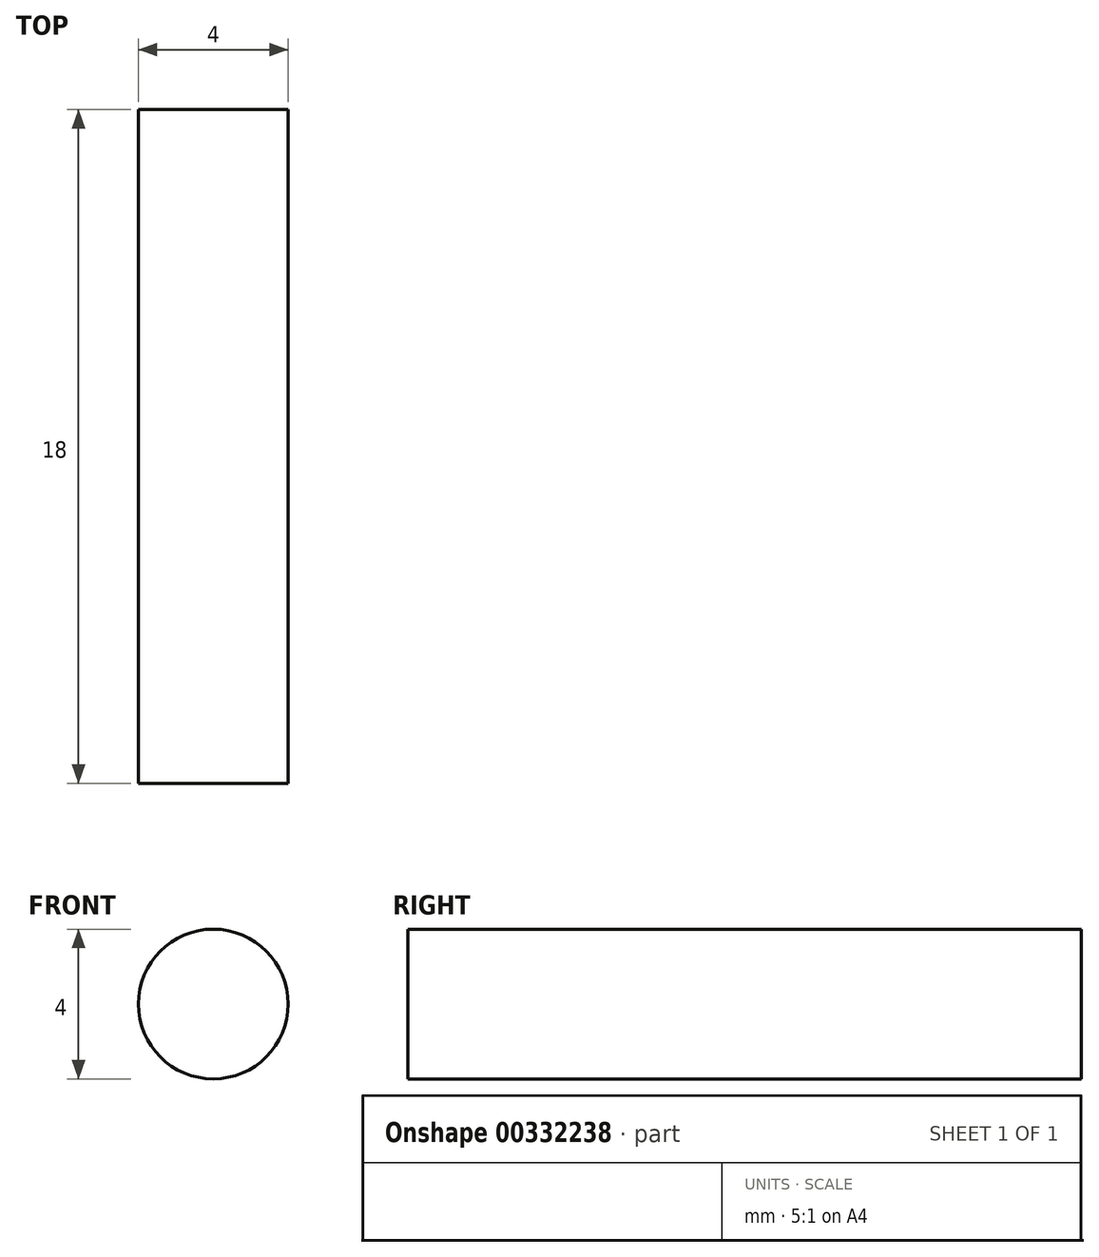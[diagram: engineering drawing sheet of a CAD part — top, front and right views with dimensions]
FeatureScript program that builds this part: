
annotation { "Feature Type Name" : "Feature", "Feature Type Description" : "" }
export const myFeature = defineFeature(function(context is Context, id is Id, definition is map)
    precondition{}
    {
        {
            var Q0;
            Q0=qCreatedBy(makeId("Front.planeOp"),FACE);
            var sketch = newSketch(context, id + "F0", { "sketchPlane" : qUnion([Q0])});
            skCircle(sketch, "E0", {"center": v(-47.7, 27.45) * mm, "radius": 2 * mm});
            skSolve(sketch);
        }
        {
            var Q0;
            Q0=makeQuery(id+"F0.imprint","IMPRINT",FACE,{"disambiguationData":[TD([[makeQuery(id+"F0.imprint","IMPRINT",EDGE,{"derivedFrom":sQuery(id+"F0.wireOp",EDGE,"E0")}),1.0]])]});
            extrude(context, id + "F1", {"entities" : qUnion([Q0]), "depth" : 63 * mm});
        }
        {
            var Q0;
            Q0=makeQuery(id+"F1.opExtrude","CAP_FACE",FACE,{"disambiguationData":[OSD([sQuery(id+"F0.wireOp",EDGE,"E0")])],"isStart":false});
            extrude(context, id + "F2", {"entities" : qUnion([Q0]), "operationType" : NewBodyOperationType.REMOVE, "oppositeDirection" : true, "depth" : 50 * mm});
        }
        {
            var Q0;
            Q0=makeQuery(id+"F2.boolean.opBoolean","COPY",FACE,{"derivedFrom":makeQuery(id+"F2.opExtrude","CAP_FACE",FACE,{"disambiguationData":[OSD([sQuery(id+"F0.wireOp",EDGE,"E0")])],"isStart":false})});
            extrude(context, id + "F3", {"entities" : qUnion([Q0]), "operationType" : NewBodyOperationType.ADD, "depth" : 15 * mm});
        }
        {
            var Q0;
            Q0=makeQuery(id+"F3.opExtrude","CAP_FACE",FACE,{"disambiguationData":[OSD([sQuery(id+"F0.wireOp",EDGE,"E0")])],"isStart":false});
            extrude(context, id + "F4", {"entities" : qUnion([Q0]), "operationType" : NewBodyOperationType.REMOVE, "oppositeDirection" : true, "depth" : 10 * mm});
        }
        {
            var Q0;
            Q0=makeQuery(id+"F4.boolean.opBoolean","COPY",FACE,{"derivedFrom":makeQuery(id+"F4.opExtrude","CAP_FACE",FACE,{"disambiguationData":[OSD([sQuery(id+"F0.wireOp",EDGE,"E0")])],"isStart":false})});
            extrude(context, id + "F5", {"entities" : qUnion([Q0]), "operationType" : NewBodyOperationType.REMOVE, "oppositeDirection" : true, "depth" : 1 * mm});
        }
        {
            var Q0;
            Q0=makeQuery(id+"F5.boolean.opBoolean","COPY",FACE,{"derivedFrom":makeQuery(id+"F5.opExtrude","CAP_FACE",FACE,{"disambiguationData":[OSD([sQuery(id+"F0.wireOp",EDGE,"E0")])],"isStart":false})});
            extrude(context, id + "F6", {"entities" : qUnion([Q0]), "operationType" : NewBodyOperationType.REMOVE, "oppositeDirection" : true, "depth" : 1 * mm});
        }
        {
            var Q0;
            Q0=makeQuery(id+"F6.boolean.opBoolean","COPY",FACE,{"derivedFrom":makeQuery(id+"F6.opExtrude","CAP_FACE",FACE,{"disambiguationData":[OSD([sQuery(id+"F0.wireOp",EDGE,"E0")])],"isStart":false})});
            extrude(context, id + "F7", {"entities" : qUnion([Q0]), "operationType" : NewBodyOperationType.ADD, "depth" : 5 * mm});
        }
        {
            var Q0;
            Q0=makeQuery(id+"F7.opExtrude","CAP_FACE",FACE,{"disambiguationData":[OSD([sQuery(id+"F0.wireOp",EDGE,"E0")])],"isStart":false});
            extrude(context, id + "F8", {"entities" : qUnion([Q0]), "operationType" : NewBodyOperationType.REMOVE, "oppositeDirection" : true, "depth" : 3 * mm});
        }
    });
